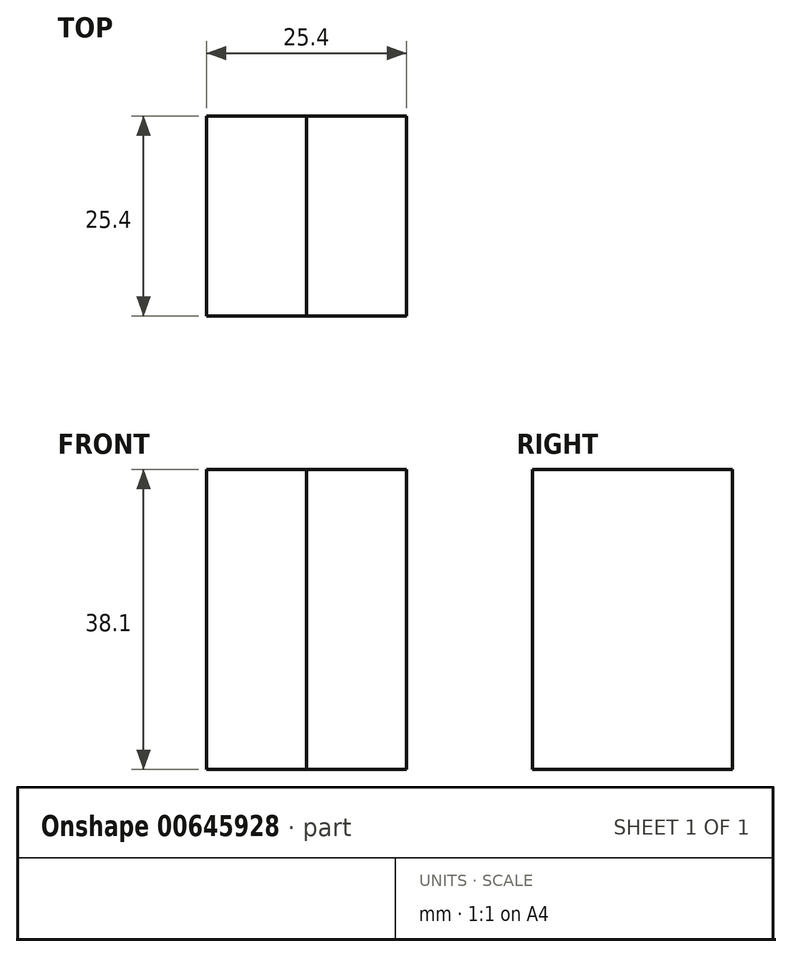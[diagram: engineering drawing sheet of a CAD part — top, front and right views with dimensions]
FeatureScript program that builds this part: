
annotation { "Feature Type Name" : "Feature", "Feature Type Description" : "" }
export const myFeature = defineFeature(function(context is Context, id is Id, definition is map)
    precondition{}
    {
        {
            var Q0;
            Q0=qCreatedBy(makeId("Front.planeOp"),FACE);
            var sketch = newSketch(context, id + "F0", { "sketchPlane" : qUnion([Q0])});
            skLineSegment(sketch, "E0.bottom", {"start": v(-12.7, 14.58) * mm, "end": v(0, 14.58) * mm});
            skLineSegment(sketch, "E0.top", {"start": v(-12.7, -23.52) * mm, "end": v(0, -23.52) * mm});
            skLineSegment(sketch, "E0.left", {"start": v(-12.7, 14.58) * mm, "end": v(-12.7, -23.52) * mm});
            skLineSegment(sketch, "E0.right", {"start": v(0, 14.58) * mm, "end": v(0, -23.52) * mm});
            skLineSegment(sketch, "E1.bottom", {"start": v(0, 14.58) * mm, "end": v(12.7, 14.58) * mm});
            skLineSegment(sketch, "E1.top", {"start": v(0, -23.52) * mm, "end": v(12.7, -23.52) * mm});
            skLineSegment(sketch, "E1.right", {"start": v(12.7, 14.58) * mm, "end": v(12.7, -23.52) * mm});
            skSolve(sketch);
        }
        {
            var Q0;
            Q0=makeQuery(id+"F0.imprint","IMPRINT",FACE,{"disambiguationData":[TD([[makeQuery(id+"F0.imprint","IMPRINT",EDGE,{"derivedFrom":sQuery(id+"F0.wireOp",EDGE,"E0.bottom")}),-1.0]])]});
            extrude(context, id + "F1", {"entities" : qUnion([Q0]), "depth" : 25.4 * mm, "offsetDistance" : 25.4 * mm});
        }
        {
            var Q0;
            Q0=makeQuery(id+"F0.imprint","IMPRINT",FACE,{"disambiguationData":[TD([[makeQuery(id+"F0.imprint","IMPRINT",EDGE,{"derivedFrom":sQuery(id+"F0.wireOp",EDGE,"E1.bottom")}),-1.0]])]});
            extrude(context, id + "F2", {"entities" : qUnion([Q0]), "depth" : 25.4 * mm, "offsetDistance" : 25.4 * mm});
        }
    });
